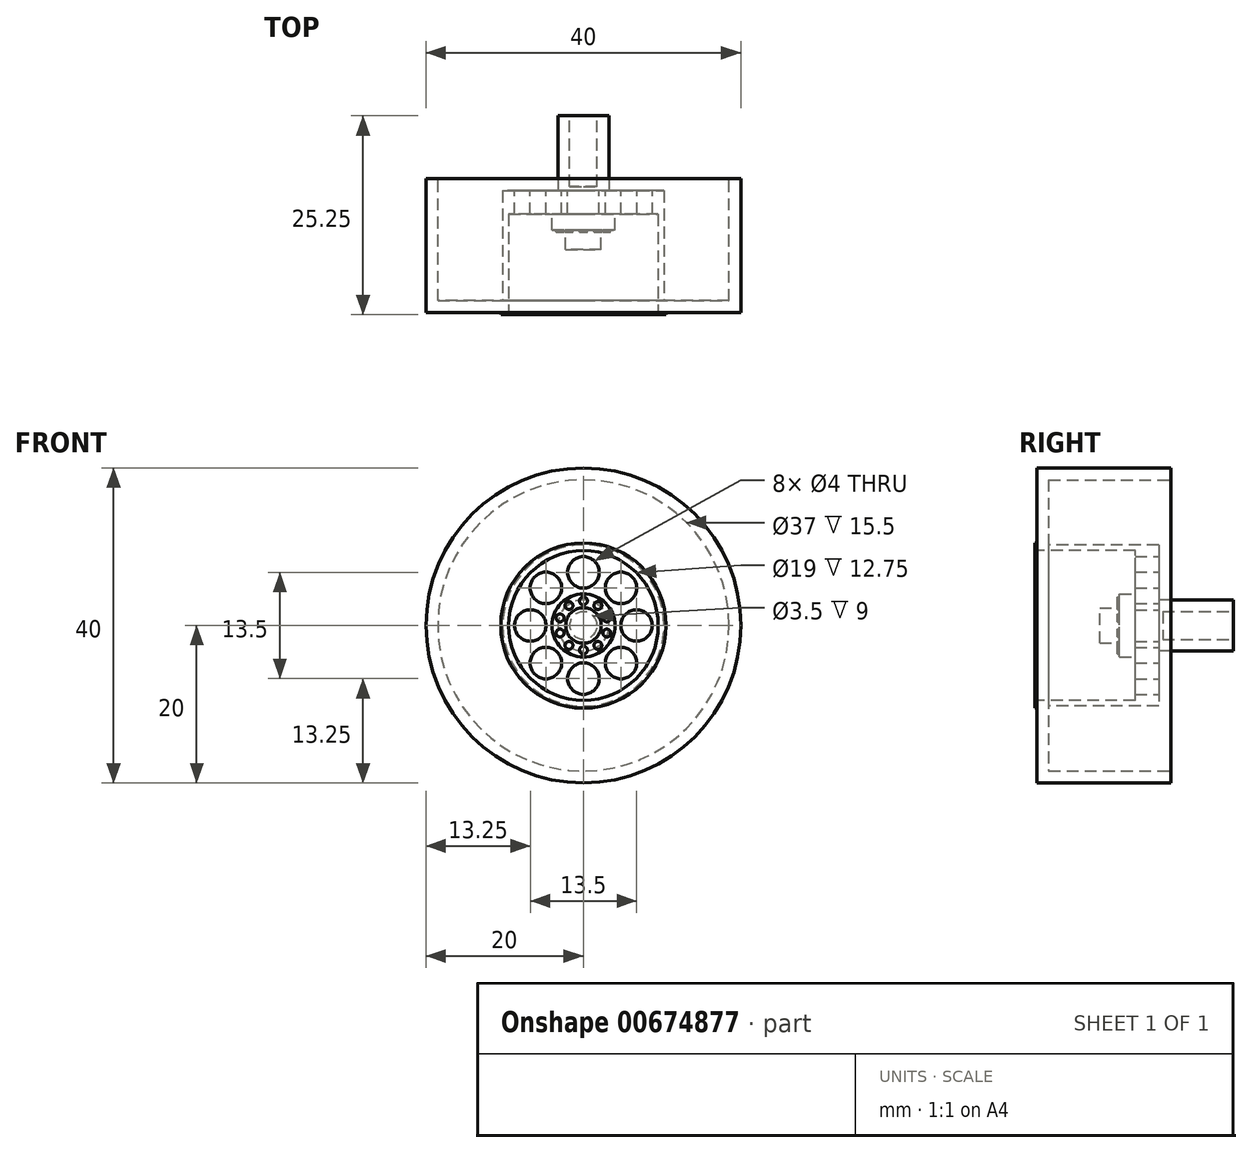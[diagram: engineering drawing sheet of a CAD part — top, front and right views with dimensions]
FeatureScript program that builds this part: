
annotation { "Feature Type Name" : "Feature", "Feature Type Description" : "" }
export const myFeature = defineFeature(function(context is Context, id is Id, definition is map)
    precondition{}
    {
        {
            var Q0;
            Q0=qCreatedBy(makeId("Front.planeOp"),FACE);
            var sketch = newSketch(context, id + "F0", { "sketchPlane" : qUnion([Q0])});
            skCircle(sketch, "E0", {"center": v(0, 0) * mm, "radius": 20 * mm});
            skSolve(sketch);
        }
        {
            var Q0;
            Q0=makeQuery(id+"F0.imprint","IMPRINT",FACE,{"disambiguationData":[TD([[makeQuery(id+"F0.imprint","IMPRINT",EDGE,{"derivedFrom":sQuery(id+"F0.wireOp",EDGE,"E0")}),1.0]])]});
            extrude(context, id + "F1", {"entities" : qUnion([Q0]), "oppositeDirection" : true, "depth" : 17 * mm, "offsetDistance" : 25 * mm});
        }
        {
            var Q0;
            Q0=makeQuery(id+"F1.opExtrude","CAP_FACE",FACE,{"disambiguationData":[OSD([sQuery(id+"F0.wireOp",EDGE,"E0")])],"isStart":false});
            var sketch = newSketch(context, id + "F2", { "sketchPlane" : qUnion([Q0])});
            skCircle(sketch, "E1", {"center": v(0, 0) * mm, "radius": 18.5 * mm});
            skSolve(sketch);
        }
        {
            var Q0;
            Q0=makeQuery(id+"F2.imprint","IMPRINT",FACE,{"disambiguationData":[TD([[makeQuery(id+"F2.imprint","IMPRINT",EDGE,{"derivedFrom":sQuery(id+"F2.wireOp",EDGE,"E1")}),1.0]])]});
            extrude(context, id + "F3", {"entities" : qUnion([Q0]), "operationType" : NewBodyOperationType.REMOVE, "oppositeDirection" : true, "depth" : 15.5 * mm, "offsetDistance" : 25 * mm});
        }
        {
            var Q0;
            Q0=makeQuery(id+"F3.boolean.opBoolean","COPY",FACE,{"derivedFrom":makeQuery(id+"F3.opExtrude","CAP_FACE",FACE,{"disambiguationData":[OSD([sQuery(id+"F2.wireOp",EDGE,"E1")])],"isStart":false})});
            var sketch = newSketch(context, id + "F4", { "sketchPlane" : qUnion([Q0])});
            skCircle(sketch, "E2", {"center": v(0, 0) * mm, "radius": 10.25 * mm});
            skSolve(sketch);
        }
        {
            var Q0;
            Q0=makeQuery(id+"F4.imprint","IMPRINT",FACE,{"disambiguationData":[TD([[makeQuery(id+"F4.imprint","IMPRINT",EDGE,{"derivedFrom":sQuery(id+"F4.wireOp",EDGE,"E2")}),1.0]])]});
            extrude(context, id + "F5", {"entities" : qUnion([Q0]), "operationType" : NewBodyOperationType.ADD, "depth" : 14 * mm, "offsetDistance" : 25 * mm});
        }
        {
            var Q0;
            Q0=makeQuery(id+"F1.opExtrude","CAP_FACE",FACE,{"disambiguationData":[OSD([sQuery(id+"F0.wireOp",EDGE,"E0")])],"isStart":true});
            var sketch = newSketch(context, id + "F6", { "sketchPlane" : qUnion([Q0])});
            skCircle(sketch, "E3", {"center": v(0, 0) * mm, "radius": 9.5 * mm});
            skSolve(sketch);
        }
        {
            var Q0;
            Q0=makeQuery(id+"F6.imprint","IMPRINT",FACE,{"disambiguationData":[TD([[makeQuery(id+"F6.imprint","IMPRINT",EDGE,{"derivedFrom":sQuery(id+"F6.wireOp",EDGE,"E3")}),1.0]])]});
            extrude(context, id + "F7", {"entities" : qUnion([Q0]), "operationType" : NewBodyOperationType.REMOVE, "oppositeDirection" : true, "depth" : 12.5 * mm, "offsetDistance" : 25 * mm});
        }
        {
            var Q0;
            Q0=makeQuery(id+"F1.opExtrude","CAP_FACE",FACE,{"disambiguationData":[OSD([sQuery(id+"F0.wireOp",EDGE,"E0")])],"isStart":true});
            var sketch = newSketch(context, id + "F8", { "sketchPlane" : qUnion([Q0])});
            skCircle(sketch, "E4", {"center": v(0, 0) * mm, "radius": 10.5 * mm});
            skSolve(sketch);
        }
        {
            var Q0;
            Q0=makeQuery(id+"F8.imprint","IMPRINT",FACE,{"disambiguationData":[TD([[makeQuery(id+"F8.imprint","IMPRINT",EDGE,{"derivedFrom":sQuery(id+"F8.wireOp",EDGE,"E4")}),1.0]])]});
            extrude(context, id + "F9", {"entities" : qUnion([Q0]), "operationType" : NewBodyOperationType.ADD, "depth" : .25 * mm, "offsetDistance" : 25 * mm});
        }
        {
            var Q0;
            Q0=makeQuery(id+"F5.opExtrude","CAP_FACE",FACE,{"disambiguationData":[OSD([sQuery(id+"F4.wireOp",EDGE,"E2")])],"isStart":false});
            var sketch = newSketch(context, id + "F10", { "sketchPlane" : qUnion([Q0])});
            skCircle(sketch, "E5", {"center": v(0, 6.75) * mm, "radius": 2 * mm});
            skCircle(sketch, "E6.1.0", {"center": v(-4.77, 4.77) * mm, "radius": 2 * mm});
            skCircle(sketch, "E6.2.0", {"center": v(-6.75, 0) * mm, "radius": 2 * mm});
            skCircle(sketch, "E6.3.0", {"center": v(-4.77, -4.77) * mm, "radius": 2 * mm});
            skCircle(sketch, "E6.4.0", {"center": v(0, -6.75) * mm, "radius": 2 * mm});
            skCircle(sketch, "E6.5.0", {"center": v(4.77, -4.77) * mm, "radius": 2 * mm});
            skCircle(sketch, "E6.6.0", {"center": v(6.75, 0) * mm, "radius": 2 * mm});
            skCircle(sketch, "E6.7.0", {"center": v(4.77, 4.77) * mm, "radius": 2 * mm});
            skPoint(sketch, "E6.center", {"position": v(0, 0) * mm});
            skCircle(sketch, "E7", {"center": v(0, 0) * mm, "radius": 3.25 * mm});
            skSolve(sketch);
        }
        {
            var Q0;
            Q0=makeQuery(id+"F10.imprint","IMPRINT",FACE,{"disambiguationData":[TD([[makeQuery(id+"F10.imprint","IMPRINT",EDGE,{"derivedFrom":sQuery(id+"F10.wireOp",EDGE,"E5")}),1.0]])]});
            var Q1;
            Q1=makeQuery(id+"F10.imprint","IMPRINT",FACE,{"disambiguationData":[TD([[makeQuery(id+"F10.imprint","IMPRINT",EDGE,{"derivedFrom":sQuery(id+"F10.wireOp",EDGE,"E6.7.0")}),1.0]])]});
            var Q2;
            Q2=makeQuery(id+"F10.imprint","IMPRINT",FACE,{"disambiguationData":[TD([[makeQuery(id+"F10.imprint","IMPRINT",EDGE,{"derivedFrom":sQuery(id+"F10.wireOp",EDGE,"E6.6.0")}),1.0]])]});
            var Q3;
            Q3=makeQuery(id+"F10.imprint","IMPRINT",FACE,{"disambiguationData":[TD([[makeQuery(id+"F10.imprint","IMPRINT",EDGE,{"derivedFrom":sQuery(id+"F10.wireOp",EDGE,"E6.5.0")}),1.0]])]});
            var Q4;
            Q4=makeQuery(id+"F10.imprint","IMPRINT",FACE,{"disambiguationData":[TD([[makeQuery(id+"F10.imprint","IMPRINT",EDGE,{"derivedFrom":sQuery(id+"F10.wireOp",EDGE,"E6.4.0")}),1.0]])]});
            var Q5;
            Q5=makeQuery(id+"F10.imprint","IMPRINT",FACE,{"disambiguationData":[TD([[makeQuery(id+"F10.imprint","IMPRINT",EDGE,{"derivedFrom":sQuery(id+"F10.wireOp",EDGE,"E6.3.0")}),1.0]])]});
            var Q6;
            Q6=makeQuery(id+"F10.imprint","IMPRINT",FACE,{"disambiguationData":[TD([[makeQuery(id+"F10.imprint","IMPRINT",EDGE,{"derivedFrom":sQuery(id+"F10.wireOp",EDGE,"E6.2.0")}),1.0]])]});
            var Q7;
            Q7=makeQuery(id+"F10.imprint","IMPRINT",FACE,{"disambiguationData":[TD([[makeQuery(id+"F10.imprint","IMPRINT",EDGE,{"derivedFrom":sQuery(id+"F10.wireOp",EDGE,"E6.1.0")}),1.0]])]});
            extrude(context, id + "F11", {"entities" : qUnion([Q0, Q1, Q2, Q3, Q4, Q5, Q6, Q7]), "operationType" : NewBodyOperationType.REMOVE, "oppositeDirection" : true, "depth" : 5 * mm, "offsetDistance" : 25 * mm});
        }
        {
            var Q0;
            Q0=makeQuery(id+"F10.imprint","IMPRINT",FACE,{"disambiguationData":[TD([[makeQuery(id+"F10.imprint","IMPRINT",EDGE,{"derivedFrom":sQuery(id+"F10.wireOp",EDGE,"E7")}),1.0]])]});
            extrude(context, id + "F12", {"entities" : qUnion([Q0]), "operationType" : NewBodyOperationType.ADD, "depth" : 9.5 * mm, "offsetDistance" : 25 * mm});
        }
        {
            var Q0;
            Q0=makeQuery(id+"F12.opExtrude","CAP_FACE",FACE,{"disambiguationData":[OSD([sQuery(id+"F10.wireOp",EDGE,"E7")])],"isStart":false});
            var sketch = newSketch(context, id + "F13", { "sketchPlane" : qUnion([Q0])});
            skCircle(sketch, "E8", {"center": v(0, 0) * mm, "radius": 1.75 * mm});
            skSolve(sketch);
        }
        {
            var Q0;
            Q0=makeQuery(id+"F13.imprint","IMPRINT",FACE,{"disambiguationData":[TD([[makeQuery(id+"F13.imprint","IMPRINT",EDGE,{"derivedFrom":sQuery(id+"F13.wireOp",EDGE,"E8")}),1.0]])]});
            extrude(context, id + "F14", {"entities" : qUnion([Q0]), "operationType" : NewBodyOperationType.REMOVE, "oppositeDirection" : true, "depth" : 9 * mm, "offsetDistance" : 25 * mm});
        }
        {
            var Q0;
            Q0=makeQuery(id+"F7.boolean.opBoolean","COPY",FACE,{"derivedFrom":makeQuery(id+"F7.opExtrude","CAP_FACE",FACE,{"disambiguationData":[OSD([sQuery(id+"F6.wireOp",EDGE,"E3")])],"isStart":false})});
            var sketch = newSketch(context, id + "F15", { "sketchPlane" : qUnion([Q0])});
            skCircle(sketch, "E9", {"center": v(0, 0) * mm, "radius": 4 * mm});
            skSolve(sketch);
        }
        {
            var Q0;
            Q0=makeQuery(id+"F15.imprint","IMPRINT",FACE,{"disambiguationData":[TD([[makeQuery(id+"F15.imprint","IMPRINT",EDGE,{"derivedFrom":sQuery(id+"F15.wireOp",EDGE,"E9")}),1.0]])]});
            extrude(context, id + "F16", {"entities" : qUnion([Q0]), "operationType" : NewBodyOperationType.ADD, "depth" : 2 * mm, "offsetDistance" : 25 * mm});
        }
        {
            var Q0;
            Q0=makeQuery(id+"F16.opExtrude","CAP_FACE",FACE,{"disambiguationData":[OSD([sQuery(id+"F15.wireOp",EDGE,"E9")])],"isStart":false});
            var sketch = newSketch(context, id + "F17", { "sketchPlane" : qUnion([Q0])});
            skCircle(sketch, "E10", {"center": v(0, 0) * mm, "radius": 2.25 * mm});
            skCircle(sketch, "E11", {"center": v(0, 3.12) * mm, "radius": 0.5 * mm});
            skCircle(sketch, "E12.1.0", {"center": v(-1.84, 2.53) * mm, "radius": 0.5 * mm});
            skCircle(sketch, "E12.2.0", {"center": v(-2.97, 0.97) * mm, "radius": 0.5 * mm});
            skCircle(sketch, "E12.3.0", {"center": v(-2.97, -0.97) * mm, "radius": 0.5 * mm});
            skCircle(sketch, "E12.4.0", {"center": v(-1.84, -2.53) * mm, "radius": 0.5 * mm});
            skCircle(sketch, "E12.5.0", {"center": v(0, -3.12) * mm, "radius": 0.5 * mm});
            skCircle(sketch, "E12.6.0", {"center": v(1.84, -2.53) * mm, "radius": 0.5 * mm});
            skCircle(sketch, "E12.7.0", {"center": v(2.97, -0.97) * mm, "radius": 0.5 * mm});
            skCircle(sketch, "E12.8.0", {"center": v(2.97, 0.97) * mm, "radius": 0.5 * mm});
            skCircle(sketch, "E12.9.0", {"center": v(1.84, 2.53) * mm, "radius": 0.5 * mm});
            skSolve(sketch);
        }
        {
            var Q0;
            Q0=makeQuery(id+"F17.imprint","IMPRINT",FACE,{"disambiguationData":[TD([[makeQuery(id+"F17.imprint","IMPRINT",EDGE,{"derivedFrom":sQuery(id+"F17.wireOp",EDGE,"E12.2.0")}),1.0]])]});
            var Q1;
            Q1=makeQuery(id+"F17.imprint","IMPRINT",FACE,{"disambiguationData":[TD([[makeQuery(id+"F17.imprint","IMPRINT",EDGE,{"derivedFrom":sQuery(id+"F17.wireOp",EDGE,"E12.1.0")}),1.0]])]});
            var Q2;
            Q2=makeQuery(id+"F17.imprint","IMPRINT",FACE,{"disambiguationData":[TD([[makeQuery(id+"F17.imprint","IMPRINT",EDGE,{"derivedFrom":sQuery(id+"F17.wireOp",EDGE,"E12.9.0")}),1.0]])]});
            var Q3;
            Q3=makeQuery(id+"F17.imprint","IMPRINT",FACE,{"disambiguationData":[TD([[makeQuery(id+"F17.imprint","IMPRINT",EDGE,{"derivedFrom":sQuery(id+"F17.wireOp",EDGE,"E11")}),1.0]])]});
            var Q4;
            Q4=makeQuery(id+"F17.imprint","IMPRINT",FACE,{"disambiguationData":[TD([[makeQuery(id+"F17.imprint","IMPRINT",EDGE,{"derivedFrom":sQuery(id+"F17.wireOp",EDGE,"E12.7.0")}),1.0]])]});
            var Q5;
            Q5=makeQuery(id+"F17.imprint","IMPRINT",FACE,{"disambiguationData":[TD([[makeQuery(id+"F17.imprint","IMPRINT",EDGE,{"derivedFrom":sQuery(id+"F17.wireOp",EDGE,"E12.6.0")}),1.0]])]});
            var Q6;
            Q6=makeQuery(id+"F17.imprint","IMPRINT",FACE,{"disambiguationData":[TD([[makeQuery(id+"F17.imprint","IMPRINT",EDGE,{"derivedFrom":sQuery(id+"F17.wireOp",EDGE,"E12.8.0")}),1.0]])]});
            var Q7;
            Q7=makeQuery(id+"F17.imprint","IMPRINT",FACE,{"disambiguationData":[TD([[makeQuery(id+"F17.imprint","IMPRINT",EDGE,{"derivedFrom":sQuery(id+"F17.wireOp",EDGE,"E12.5.0")}),1.0]])]});
            var Q8;
            Q8=makeQuery(id+"F17.imprint","IMPRINT",FACE,{"disambiguationData":[TD([[makeQuery(id+"F17.imprint","IMPRINT",EDGE,{"derivedFrom":sQuery(id+"F17.wireOp",EDGE,"E12.3.0")}),1.0]])]});
            var Q9;
            Q9=makeQuery(id+"F17.imprint","IMPRINT",FACE,{"disambiguationData":[TD([[makeQuery(id+"F17.imprint","IMPRINT",EDGE,{"derivedFrom":sQuery(id+"F17.wireOp",EDGE,"E12.4.0")}),1.0]])]});
            extrude(context, id + "F18", {"entities" : qUnion([Q0, Q1, Q2, Q3, Q4, Q5, Q6, Q7, Q8, Q9]), "operationType" : NewBodyOperationType.ADD, "depth" : 0.25 * mm, "offsetDistance" : 25 * mm});
        }
        {
            var Q0;
            Q0=makeQuery(id+"F17.imprint","IMPRINT",FACE,{"disambiguationData":[TD([[makeQuery(id+"F17.imprint","IMPRINT",EDGE,{"derivedFrom":sQuery(id+"F17.wireOp",EDGE,"E10")}),1.0]])]});
            extrude(context, id + "F19", {"entities" : qUnion([Q0]), "operationType" : NewBodyOperationType.ADD, "depth" : 2.5 * mm, "offsetDistance" : 25 * mm});
        }
    });
